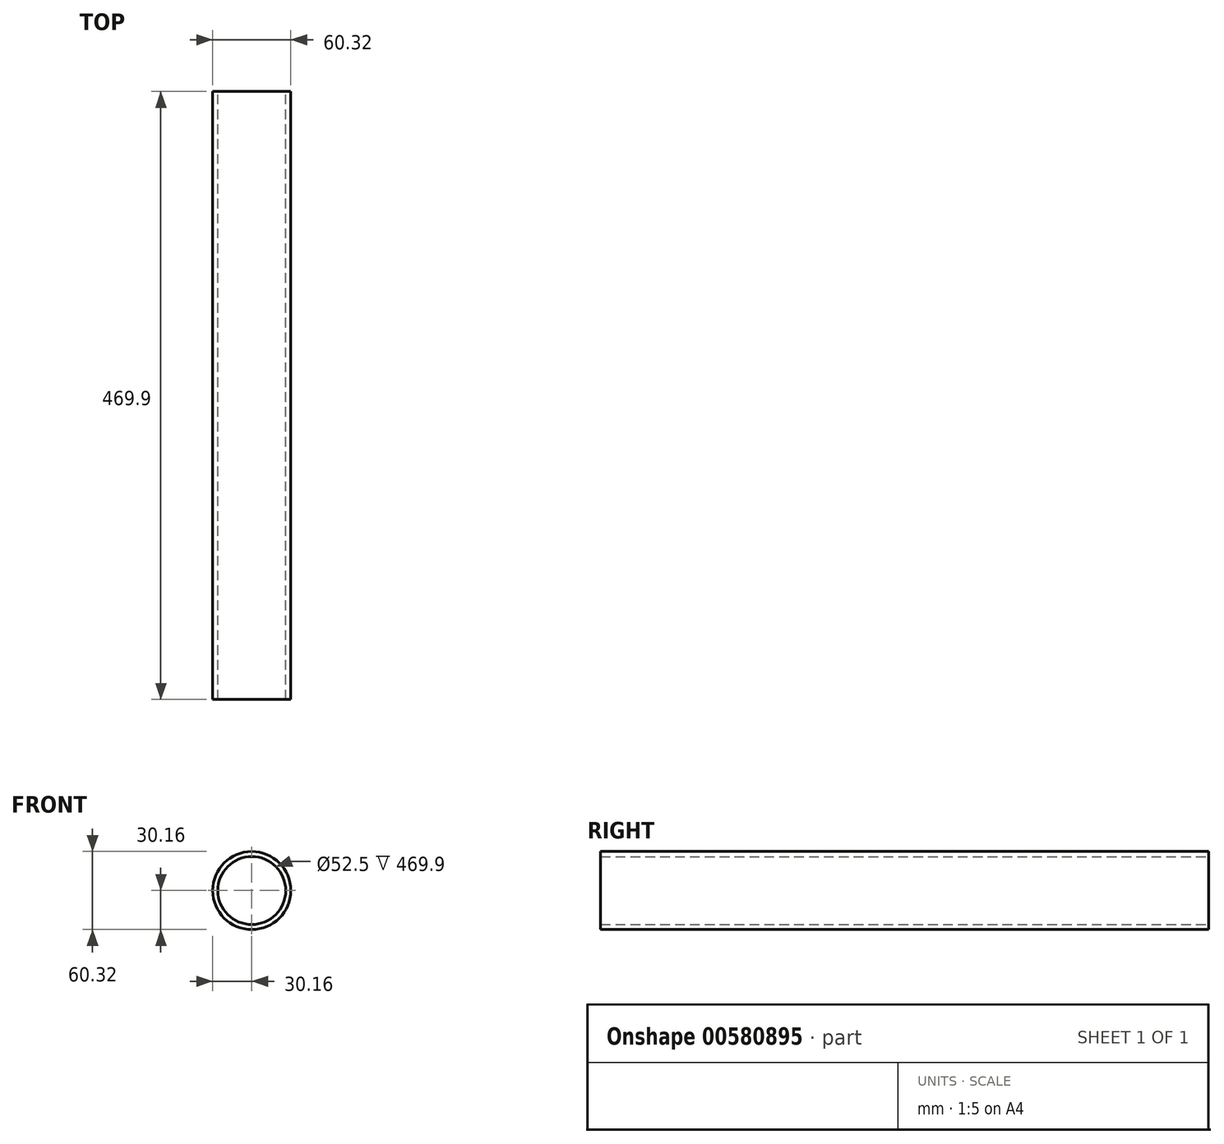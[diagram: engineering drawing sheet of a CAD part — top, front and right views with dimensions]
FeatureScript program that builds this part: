
annotation { "Feature Type Name" : "Feature", "Feature Type Description" : "" }
export const myFeature = defineFeature(function(context is Context, id is Id, definition is map)
    precondition{}
    {
        {
            var Q0;
            Q0=qCreatedBy(makeId("Front.planeOp"),FACE);
            var sketch = newSketch(context, id + "F0", { "sketchPlane" : qUnion([Q0])});
            skCircle(sketch, "E0", {"center": v(0, 0) * mm, "radius": 30.16 * mm});
            skCircle(sketch, "E1.0", {"center": v(0, 0) * mm, "radius": 26.25 * mm});
            skSolve(sketch);
        }
        {
            var Q0;
            Q0 = qSketchRegion(id + "F0", true);
            extrude(context, id + "F1", {"entities" : qUnion([Q0]), "endBound" : BoundingType.SYMMETRIC, "depth" : 469.9 * mm, "offsetDistance" : 25 * mm});
        }
    });
